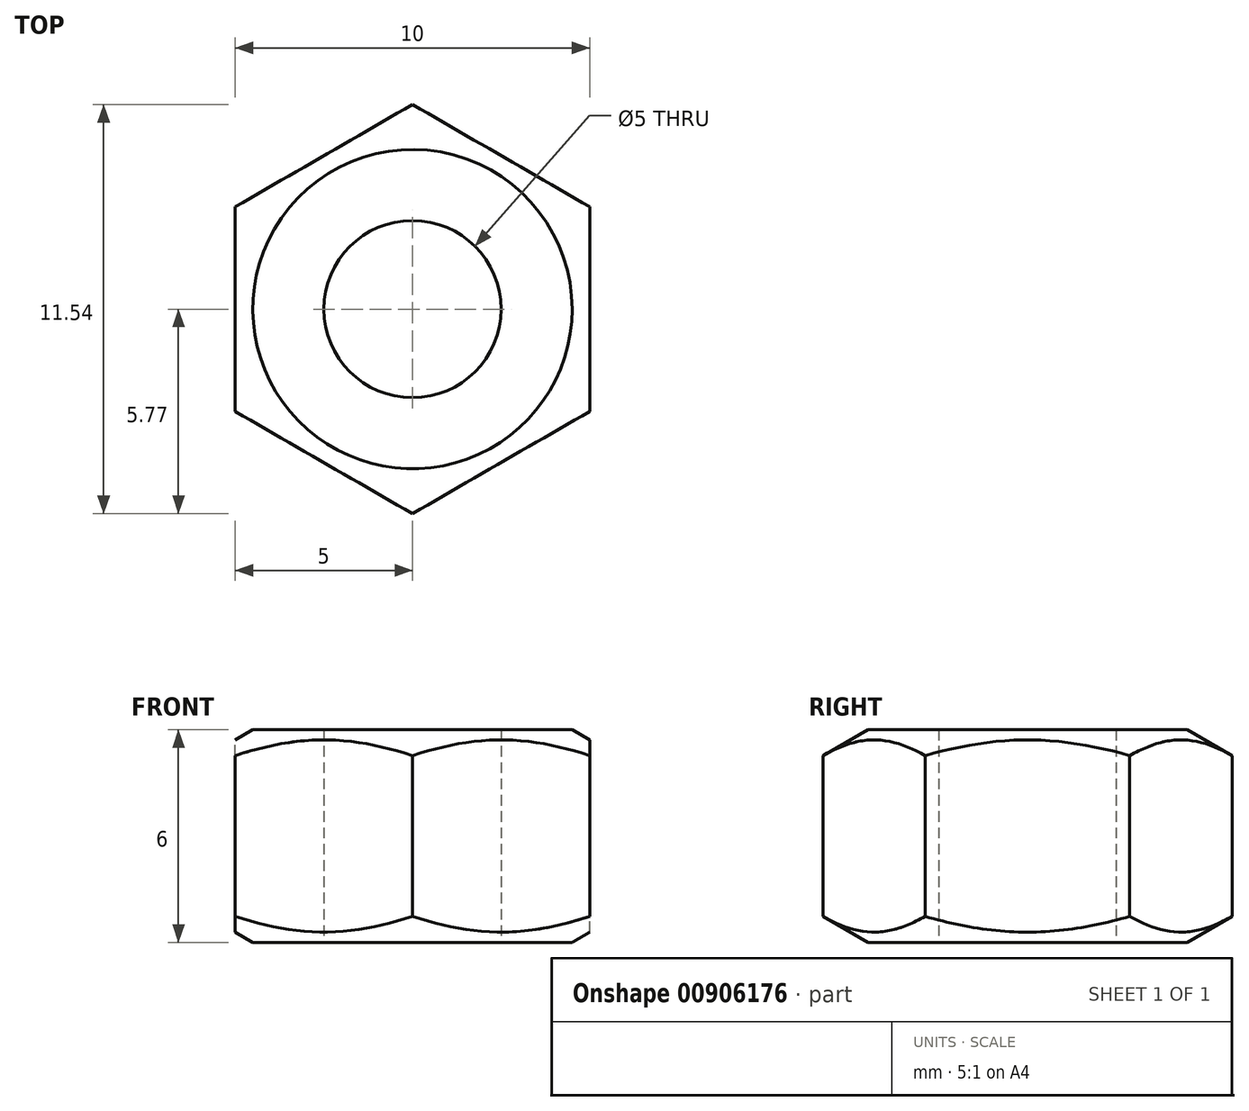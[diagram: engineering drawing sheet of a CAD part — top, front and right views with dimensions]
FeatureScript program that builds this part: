
annotation { "Feature Type Name" : "Feature", "Feature Type Description" : "" }
export const myFeature = defineFeature(function(context is Context, id is Id, definition is map)
    precondition{}
    {
        {
            var Q0;
            Q0=qCreatedBy(makeId("Top.planeOp"),FACE);
            var sketch = newSketch(context, id + "F0", { "sketchPlane" : qUnion([Q0])});
            skCircle(sketch, "E0.cCircle", {"center": v(0, 0) * mm, "radius": 5 * mm, "construction": true});
            skLineSegment(sketch, "E0.0", {"start": v(-5, -2.89) * mm, "end": v(-5, 2.89) * mm});
            skLineSegment(sketch, "E0.1", {"start": v(-5, 2.89) * mm, "end": v(0, 5.77) * mm});
            skLineSegment(sketch, "E0.2", {"start": v(0, 5.77) * mm, "end": v(5, 2.89) * mm});
            skLineSegment(sketch, "E0.3", {"start": v(5, 2.89) * mm, "end": v(5, -2.89) * mm});
            skLineSegment(sketch, "E0.4", {"start": v(5, -2.89) * mm, "end": v(0, -5.77) * mm});
            skLineSegment(sketch, "E0.5", {"start": v(0, -5.77) * mm, "end": v(-5, -2.89) * mm});
            skPoint(sketch, "E0.0.midPoint", {"position": v(-5, 0) * mm});
            skCircle(sketch, "E1", {"center": v(0, 0) * mm, "radius": 2.5 * mm});
            skSolve(sketch);
        }
        {
            var Q0;
            Q0 = qSketchRegion(id + "F0", true);
            extrude(context, id + "F1", {"entities" : qUnion([Q0]), "depth" : 6 * mm, "offsetDistance" : 25 * mm});
        }
        {
            var Q0;
            Q0=qCreatedBy(makeId("Front.planeOp"),FACE);
            var sketch = newSketch(context, id + "F2", { "sketchPlane" : qUnion([Q0])});
            skLineSegment(sketch, "E2", {"start": v(0, 8.6) * mm, "end": v(-9.7, 3) * mm});
            skLineSegment(sketch, "E3", {"start": v(-9.7, 3) * mm, "end": v(0, -2.6) * mm});
            skLineSegment(sketch, "E4", {"start": v(0, -2.6) * mm, "end": v(0, 8.6) * mm});
            skLineSegment(sketch, "E5", {"start": v(0, 3) * mm, "end": v(-9.7, 3) * mm, "construction": true});
            skSolve(sketch);
        }
        {
            var Q0;
            Q0 = qSketchRegion(id + "F2", true);
            var Q1;
            Q1=sQuery(id+"F2.wireOp",EDGE,"E4");
            revolve(context, id + "F3", {"operationType" : NewBodyOperationType.INTERSECT, "surfaceOperationType" : NewSurfaceOperationType.NEW, "entities" : qUnion([Q0]), "axis" : qUnion([Q1]), "revolveType" : RevolveType.FULL, "oppositeDirection" : true});
        }
    });
